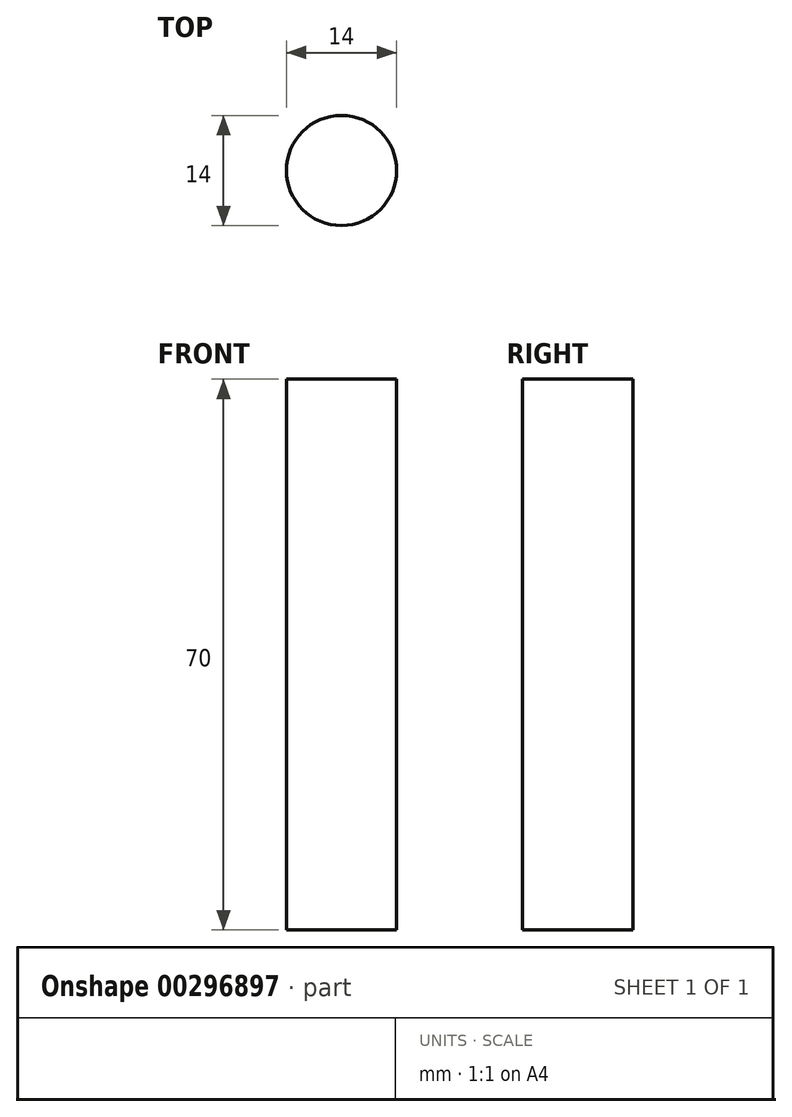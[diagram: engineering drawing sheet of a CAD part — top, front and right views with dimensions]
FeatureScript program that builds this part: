
annotation { "Feature Type Name" : "Feature", "Feature Type Description" : "" }
export const myFeature = defineFeature(function(context is Context, id is Id, definition is map)
    precondition{}
    {
        {
            var Q0;
            Q0=qCreatedBy(makeId("Top.planeOp"),FACE);
            var sketch = newSketch(context, id + "F0", { "sketchPlane" : qUnion([Q0])});
            skCircle(sketch, "E0", {"center": v(0, 0) * mm, "radius": 7 * mm});
            skSolve(sketch);
        }
        {
            var Q0;
            Q0 = qSketchRegion(id + "F0", true);
            extrude(context, id + "F1", {"entities" : qUnion([Q0]), "depth" : 70 * mm});
        }
    });
